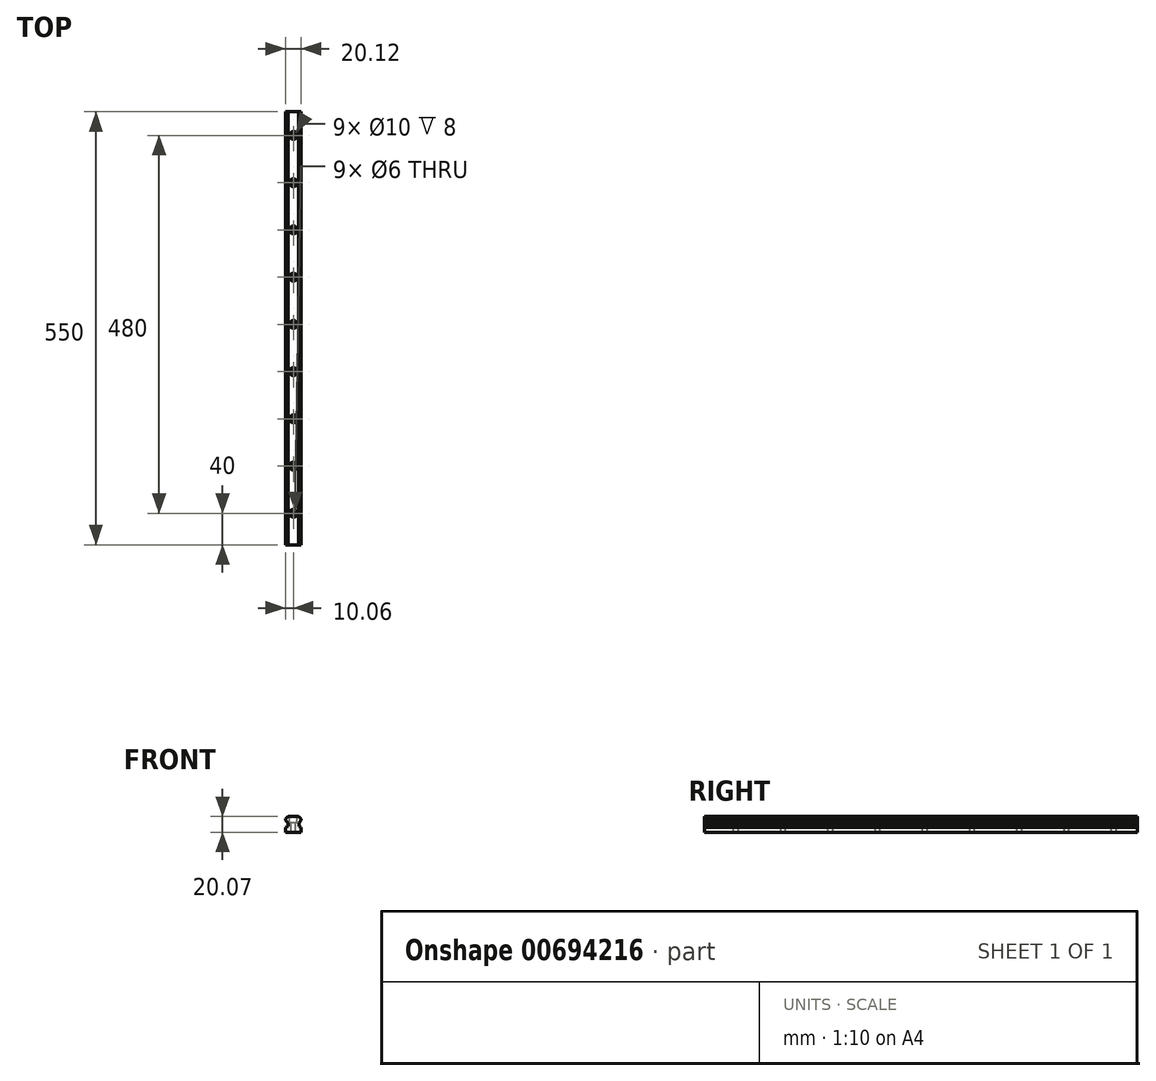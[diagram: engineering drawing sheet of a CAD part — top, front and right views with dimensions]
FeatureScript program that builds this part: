
annotation { "Feature Type Name" : "Feature", "Feature Type Description" : "" }
export const myFeature = defineFeature(function(context is Context, id is Id, definition is map)
    precondition{}
    {
        {
            var Q0;
            Q0=qCreatedBy(makeId("Front.planeOp"),FACE);
            var sketch = newSketch(context, id + "F0", { "sketchPlane" : qUnion([Q0])});
            skLineSegment(sketch, "E0.1", {"start": v(-10.05, 14.63) * mm, "end": v(-10.06, 16.92) * mm});
            skLineSegment(sketch, "E0.2", {"start": v(-6.9, 11.59) * mm, "end": v(-10.05, 14.63) * mm});
            skLineSegment(sketch, "E0.3", {"start": v(-6.95, 7.28) * mm, "end": v(-6.9, 11.59) * mm});
            skLineSegment(sketch, "E0.5", {"start": v(-10.06, 16.92) * mm, "end": v(-6.7, 20.07) * mm});
            skLineSegment(sketch, "E0.6", {"start": v(0, 20.07) * mm, "end": v(-6.7, 20.07) * mm});
            skLineSegment(sketch, "E1", {"start": v(10, 0) * mm, "end": v(10, 6.01) * mm});
            skLineSegment(sketch, "E2.MirrorCS", {"start": v(10.06, 16.92) * mm, "end": v(6.7, 20.07) * mm});
            skLineSegment(sketch, "E3.MirrorCS", {"start": v(0, 20.07) * mm, "end": v(6.7, 20.07) * mm});
            skLineSegment(sketch, "E4.MirrorCS", {"start": v(10.05, 14.63) * mm, "end": v(10.06, 16.92) * mm});
            skLineSegment(sketch, "E5.MirrorCS", {"start": v(6.56, 11.26) * mm, "end": v(10.05, 14.63) * mm});
            skLineSegment(sketch, "E6.MirrorCS", {"start": v(6.95, 7.28) * mm, "end": v(6.88, 12.66) * mm});
            skLineSegment(sketch, "E7.MirrorCS", {"start": v(10, 6.01) * mm, "end": v(6.95, 7.28) * mm});
            skLineSegment(sketch, "E8", {"start": v(10, 0) * mm, "end": v(0, 0) * mm});
            skLineSegment(sketch, "E9", {"start": v(0, 0) * mm, "end": v(-10, 0) * mm});
            skLineSegment(sketch, "E10", {"start": v(-10, 0) * mm, "end": v(-10, 6.01) * mm});
            skLineSegment(sketch, "E11", {"start": v(-10, 6.01) * mm, "end": v(-6.95, 7.28) * mm});
            skPoint(sketch, "E12.orphan", {"position": v(-6.88, 12.66) * mm});
            skPoint(sketch, "E13.orphan", {"position": v(-6.56, 11.26) * mm});
            skSolve(sketch);
        }
        {
            var Q0;
            Q0 = qSketchRegion(id + "F0", true);
            extrude(context, id + "F1", {"entities" : qUnion([Q0]), "depth" : 550 * mm, "offsetDistance" : 25 * mm});
        }
        {
            var Q0;
            Q0=makeQuery(id+"F1.opExtrude","SWEPT_FACE",FACE,{"disambiguationData":[OSD([sQuery(id+"F0.wireOp",EDGE,"E0.6"),sQuery(id+"F0.wireOp",EDGE,"E3.MirrorCS")])]});
            var sketch = newSketch(context, id + "F2", { "sketchPlane" : qUnion([Q0])});
            skCircle(sketch, "E14", {"center": v(0, -510) * mm, "radius": 5 * mm});
            skPoint(sketch, "E14.centerSnap0", {"position": v(0, -550) * mm});
            skCircle(sketch, "E15.0.1.0", {"center": v(0, -450) * mm, "radius": 5 * mm});
            skCircle(sketch, "E15.0.2.0", {"center": v(0, -390) * mm, "radius": 5 * mm});
            skCircle(sketch, "E15.0.3.0", {"center": v(0, -330) * mm, "radius": 5 * mm});
            skCircle(sketch, "E15.0.4.0", {"center": v(0, -270) * mm, "radius": 5 * mm});
            skCircle(sketch, "E15.0.5.0", {"center": v(0, -210) * mm, "radius": 5 * mm});
            skCircle(sketch, "E15.0.6.0", {"center": v(0, -150) * mm, "radius": 5 * mm});
            skCircle(sketch, "E15.0.7.0", {"center": v(0, -90) * mm, "radius": 5 * mm});
            skCircle(sketch, "E15.0.8.0", {"center": v(0, -30) * mm, "radius": 5 * mm});
            skLineSegment(sketch, "E15.direction1", {"start": v(0, -510) * mm, "end": v(25, -510) * mm, "construction": true});
            skLineSegment(sketch, "E15.direction2", {"start": v(0, -510) * mm, "end": v(0, -450) * mm, "construction": true});
            skSolve(sketch);
        }
        {
            var Q0;
            Q0 = qSketchRegion(id + "F2", true);
            extrude(context, id + "F3", {"entities" : qUnion([Q0]), "operationType" : NewBodyOperationType.REMOVE, "oppositeDirection" : true, "depth" : 8 * mm, "offsetDistance" : 25 * mm});
        }
        {
            var Q0;
            Q0=makeQuery(id+"F3.boolean.opBoolean","COPY",FACE,{"derivedFrom":makeQuery(id+"F3.opExtrude","CAP_FACE",FACE,{"disambiguationData":[OSD([sQuery(id+"F2.wireOp",EDGE,"E14")])],"isStart":false})});
            var sketch = newSketch(context, id + "F4", { "sketchPlane" : qUnion([Q0])});
            skCircle(sketch, "E16", {"center": v(0, -510) * mm, "radius": 3 * mm});
            skCircle(sketch, "E17.0.1.0", {"center": v(0, -450) * mm, "radius": 3 * mm});
            skCircle(sketch, "E17.0.2.0", {"center": v(0, -390) * mm, "radius": 3 * mm});
            skCircle(sketch, "E17.0.3.0", {"center": v(0, -330) * mm, "radius": 3 * mm});
            skCircle(sketch, "E17.0.4.0", {"center": v(0, -270) * mm, "radius": 3 * mm});
            skCircle(sketch, "E17.0.5.0", {"center": v(0, -210) * mm, "radius": 3 * mm});
            skCircle(sketch, "E17.0.6.0", {"center": v(0, -150) * mm, "radius": 3 * mm});
            skCircle(sketch, "E17.0.7.0", {"center": v(0, -90) * mm, "radius": 3 * mm});
            skCircle(sketch, "E17.0.8.0", {"center": v(0, -30) * mm, "radius": 3 * mm});
            skLineSegment(sketch, "E17.direction1", {"start": v(0, -510) * mm, "end": v(25, -510) * mm, "construction": true});
            skLineSegment(sketch, "E17.direction2", {"start": v(0, -510) * mm, "end": v(0, -450) * mm, "construction": true});
            skSolve(sketch);
        }
        {
            var Q0;
            Q0=makeQuery(id+"F4.imprint","IMPRINT",FACE,{"disambiguationData":[TD([[makeQuery(id+"F4.imprint","IMPRINT",EDGE,{"derivedFrom":sQuery(id+"F4.wireOp",EDGE,"E16")}),1.0]])]});
            var Q1;
            Q1=makeQuery(id+"F4.imprint","IMPRINT",FACE,{"disambiguationData":[TD([[makeQuery(id+"F4.imprint","IMPRINT",EDGE,{"derivedFrom":sQuery(id+"F4.wireOp",EDGE,"E17.0.1.0")}),1.0]])]});
            var Q2;
            Q2=makeQuery(id+"F4.imprint","IMPRINT",FACE,{"disambiguationData":[TD([[makeQuery(id+"F4.imprint","IMPRINT",EDGE,{"derivedFrom":sQuery(id+"F4.wireOp",EDGE,"E17.0.2.0")}),1.0]])]});
            var Q3;
            Q3=makeQuery(id+"F4.imprint","IMPRINT",FACE,{"disambiguationData":[TD([[makeQuery(id+"F4.imprint","IMPRINT",EDGE,{"derivedFrom":sQuery(id+"F4.wireOp",EDGE,"E17.0.3.0")}),1.0]])]});
            var Q4;
            Q4=makeQuery(id+"F4.imprint","IMPRINT",FACE,{"disambiguationData":[TD([[makeQuery(id+"F4.imprint","IMPRINT",EDGE,{"derivedFrom":sQuery(id+"F4.wireOp",EDGE,"E17.0.4.0")}),1.0]])]});
            var Q5;
            Q5=makeQuery(id+"F4.imprint","IMPRINT",FACE,{"disambiguationData":[TD([[makeQuery(id+"F4.imprint","IMPRINT",EDGE,{"derivedFrom":sQuery(id+"F4.wireOp",EDGE,"E17.0.5.0")}),1.0]])]});
            var Q6;
            Q6=makeQuery(id+"F4.imprint","IMPRINT",FACE,{"disambiguationData":[TD([[makeQuery(id+"F4.imprint","IMPRINT",EDGE,{"derivedFrom":sQuery(id+"F4.wireOp",EDGE,"E17.0.6.0")}),1.0]])]});
            var Q7;
            Q7=makeQuery(id+"F4.imprint","IMPRINT",FACE,{"disambiguationData":[TD([[makeQuery(id+"F4.imprint","IMPRINT",EDGE,{"derivedFrom":sQuery(id+"F4.wireOp",EDGE,"E17.0.8.0")}),1.0]])]});
            var Q8;
            Q8=makeQuery(id+"F4.imprint","IMPRINT",FACE,{"disambiguationData":[TD([[makeQuery(id+"F4.imprint","IMPRINT",EDGE,{"derivedFrom":sQuery(id+"F4.wireOp",EDGE,"E17.0.7.0")}),1.0]])]});
            extrude(context, id + "F5", {"entities" : qUnion([Q0, Q1, Q2, Q3, Q4, Q5, Q6, Q7, Q8]), "operationType" : NewBodyOperationType.REMOVE, "oppositeDirection" : true, "depth" : 25 * mm, "offsetDistance" : 25 * mm});
        }
    });
